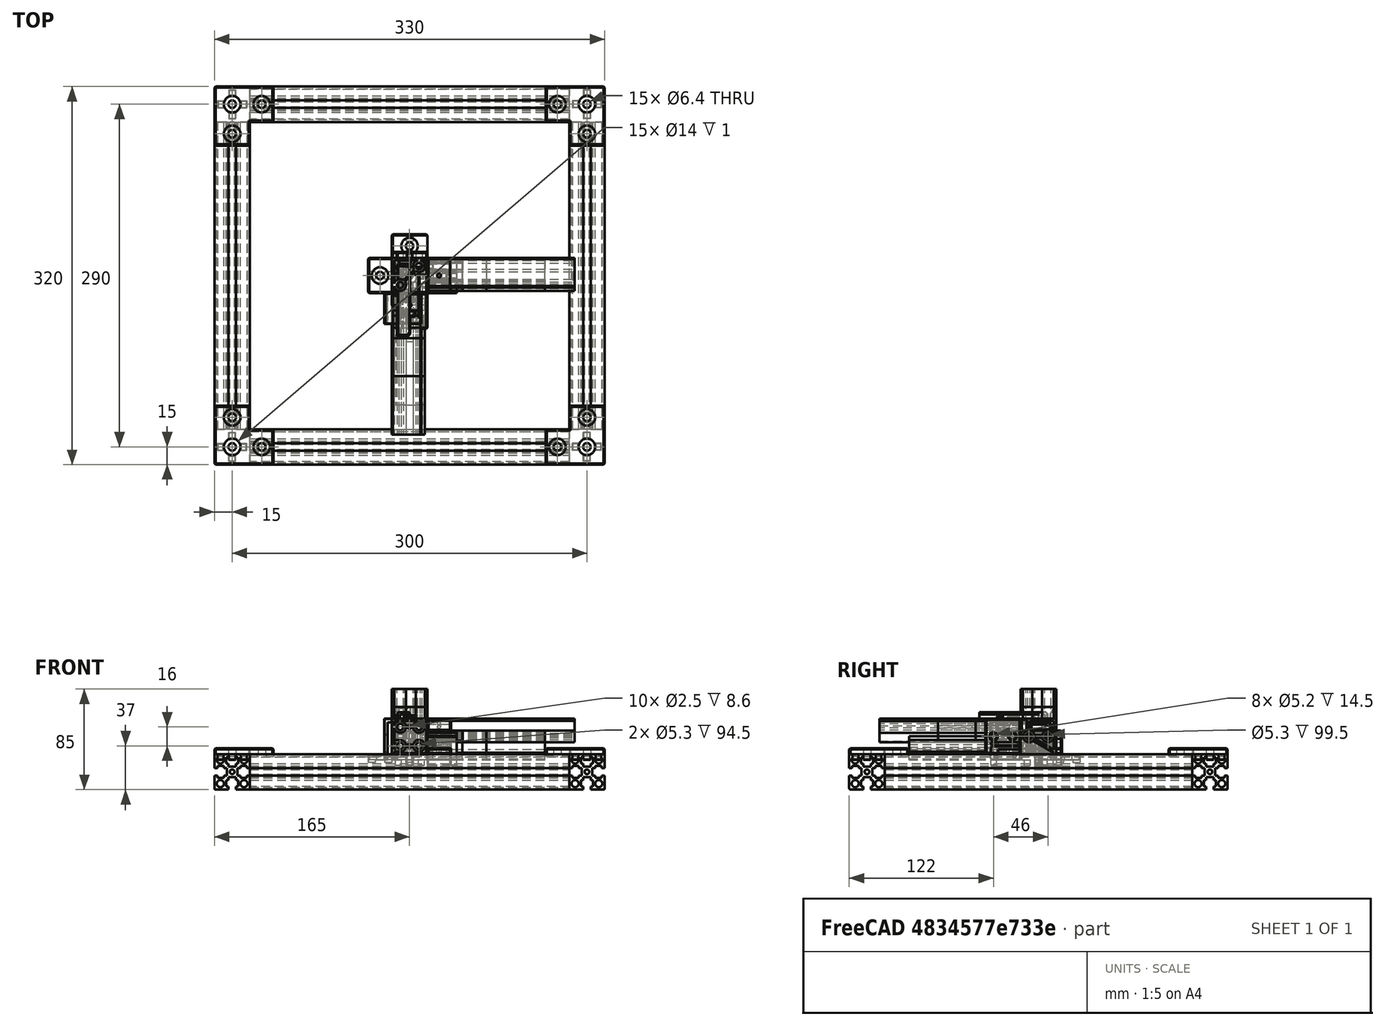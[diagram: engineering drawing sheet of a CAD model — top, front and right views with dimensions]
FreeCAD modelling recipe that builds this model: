
FCSTD DOCUMENT  (FreeCAD 0.18R16146 (Git))
Label: hophat-CF
License: All rights reserved
LicenseURL: http://en.wikipedia.org/wiki/All_rights_reserved
objects: Part::Cylinder×112, Part::MultiFuse×82, Part::Box×79, Part::Chamfer×76, Part::Feature×58, Part::Cut×58, Part::MultiCommon×4, App::DocumentObjectGroup×1
note: 469 computed .brp shape members not serialized (recipe doc carries the construction recipe); baked Part::Feature solids carry a one-line shape summary decoded from their .brp

FEATURE [Part::Feature] Fusion025  label="extrusion-260-003"
  Placement = pos=(-150,-130,350) rot=(-1,0,0;1.5708rad)
  shape: bbox 30 x 260 x 30 mm, 63 faces (baked)
FEATURE [Part::Feature] Fusion032  label="extrusion-270-005"
  Placement = pos=(-135,-145,350) rot=(0,1,0;1.5708rad)
  shape: bbox 270 x 30 x 30 mm, 63 faces (baked)
FEATURE [Part::Feature] Fusion026  label="extrusion-260-004"
  Placement = pos=(150,-130,350) rot=(-1,0,0;1.5708rad)
  shape: bbox 30 x 260 x 30 mm, 63 faces (baked)
FEATURE [Part::Feature] Fusion031  label="extrusion-270-004"
  Placement = pos=(-135,145,350) rot=(0,1,0;1.5708rad)
  shape: bbox 270 x 30 x 30 mm, 63 faces (baked)
FEATURE [Part::MultiFuse] Fusion004003058  label="__top-framr-pref"
  Placement = pos=(0,0,-365) rot=(0,0,1;0rad)
  Shapes = -> [Fusion025,Fusion031,Fusion026,Fusion032]
FEATURE [Part::Feature] Fusion020006007003002004  label="top-joiner-002"
  Placement = pos=(-150,-145,370) rot=(0.707107,0.707107,0;3.14159rad)
  shape: bbox 50 x 50 x 10 mm, 87 faces (baked)
FEATURE [Part::Feature] Fusion020006007003002005  label="top-joiner-003"
  Placement = pos=(-150,145,370) rot=(1,0,0;3.14159rad)
  shape: bbox 50 x 50 x 10 mm, 87 faces (baked)
FEATURE [Part::Feature] Fusion020006007003002006  label="top-joiner-004"
  Placement = pos=(150,145,370) rot=(0.707107,-0.707107,0;3.14159rad)
  shape: bbox 50 x 50 x 10 mm, 87 faces (baked)
FEATURE [Part::Feature] Fusion020006007003002007  label="top-joiner-001"
  Placement = pos=(150,-145,370) rot=(0,1,0;3.14159rad)
  shape: bbox 50 x 50 x 10 mm, 87 faces (baked)
FEATURE [Part::Cylinder] Cylinder
  Angle = 360
  AttacherType = Attacher::AttachEngine3D
  Height = 10
  Radius = 1.25
FEATURE [Part::Cylinder] Cylinder001
  Angle = 360
  AttacherType = Attacher::AttachEngine3D
  Height = 3
  Placement = pos=(0,0,10) rot=(0,0,1;0rad)
  Radius = 3
FEATURE [Part::MultiFuse] Fusion020006007003002009  label="_M3-self-tapping"
  Shapes = -> [Cylinder001,Cylinder]
FEATURE [Part::Cylinder] Cylinder002
  Angle = 360
  AttacherType = Attacher::AttachEngine3D
  Height = 10
  Radius = 1.65
FEATURE [Part::Cylinder] Cylinder003
  Angle = 360
  AttacherType = Attacher::AttachEngine3D
  Height = 3
  Placement = pos=(0,0,10) rot=(0,0,1;0rad)
  Radius = 3
FEATURE [Part::MultiFuse] Fusion020006007003002010  label="_M3-outer-slot"
  Shapes = -> [Cylinder002,Cylinder003]
FEATURE [Part::MultiFuse] Fusion020006007003002008  label="__top-joiner-pref"
  Placement = pos=(0,0,-365) rot=(0,0,1;0rad)
  Shapes = -> [Fusion020006007003002007,Fusion020006007003002004,Fusion020006007003002006,Fusion020006007003002005]
FEATURE [Part::Feature] Fusion020006007003002011  label="top-joiner-005"
  Placement = pos=(-5.7e-14,0,0) rot=(0,1,0;3.14159rad)
  shape: bbox 50 x 50 x 10 mm, 87 faces (baked)
FEATURE [App::DocumentObjectGroup] Group  label="Preference"
  Group = -> [Fusion020006007003002011,Fusion020006007003002008,Fusion020006007003002010,Fusion020006007003002009,Fusion004003058]
FEATURE [Part::Box] Box  label="Cube"
  AttacherType = Attacher::AttachEngine3D
  Height = 30
  Length = 30
  Placement = pos=(-15,-15,0) rot=(0,0,1;0rad)
  Width = 30
FEATURE [Part::Cylinder] Cylinder004
  Angle = 360
  AttacherType = Attacher::AttachEngine3D
  Height = 10
  Placement = pos=(-8,-8,0) rot=(0,0,1;0rad)
  Radius = 2.5
FEATURE [Part::Cylinder] Cylinder005
  Angle = 360
  AttacherType = Attacher::AttachEngine3D
  Height = 10
  Placement = pos=(8,8,0) rot=(0,0,1;0rad)
  Radius = 2.5
FEATURE [Part::Box] Box001  label="Cube001"
  AttacherType = Attacher::AttachEngine3D
  Height = 10
  Length = 10
  Placement = pos=(9.54594,8.83883,20) rot=(0,0,1;0.785398rad)
  Width = 1
FEATURE [Part::Box] Box002  label="Cube002"
  AttacherType = Attacher::AttachEngine3D
  Height = 10
  Length = 10
  Placement = pos=(-15.9099,-16.617,20) rot=(0,0,1;0.785398rad)
  Width = 1
FEATURE [Part::MultiFuse] Fusion020006007003002012
  Shapes = -> [Box002,Box001]
FEATURE [Part::MultiFuse] Fusion
  Placement = pos=(0,0,20) rot=(0,0,1;0rad)
  Shapes = -> [Cylinder004,Cylinder005]
FEATURE [Part::Chamfer] Chamfer
  Base = -> Box
  Edges = 12 edges r=1: [Edge1,Edge2,Edge3,Edge4,Edge5,Edge6,Edge7,Edge8,Edge9,Edge10,Edge11,Edge12]
FEATURE [Part::Cut] Cut
  Base = -> Chamfer
  Tool = -> Fusion
FEATURE [Part::Cut] Cut001
  Base = -> Cut
  Tool = -> Fusion020006007003002012
FEATURE [Part::Cylinder] Cylinder006
  Angle = 360
  AttacherType = Attacher::AttachEngine3D
  Height = 21
  Placement = pos=(-8,5.5,7) rot=(1,0,0;1.5708rad)
  Radius = 2.5
FEATURE [Part::Cylinder] Cylinder007
  Angle = 360
  AttacherType = Attacher::AttachEngine3D
  Height = 21
  Placement = pos=(8,5.5,7) rot=(1,0,0;1.5708rad)
  Radius = 2.5
FEATURE [Part::MultiFuse] Fusion020006007003002013
  Shapes = -> [Cylinder006,Cylinder007]
FEATURE [Part::Cylinder] Cylinder008
  Angle = 360
  AttacherType = Attacher::AttachEngine3D
  Height = 5
  Radius = 6
FEATURE [Part::Cut] Cut002
  Base = -> Cut001
  Tool = -> Cylinder008
FEATURE [Part::Cut] Cut003
  Base = -> Cut002
  Tool = -> Fusion020006007003002013
FEATURE [Part::Box] Box003  label="Cube003"
  AttacherType = Attacher::AttachEngine3D
  Height = 5
  Length = 1
  Placement = pos=(-8.5,-35,0) rot=(0,0,1;0rad)
  Width = 21
FEATURE [Part::Box] Box004  label="Cube004"
  AttacherType = Attacher::AttachEngine3D
  Height = 5
  Length = 1
  Placement = pos=(7.5,-35,0) rot=(0,0,1;0rad)
  Width = 21
FEATURE [Part::Cylinder] Cylinder009
  Angle = 360
  AttacherType = Attacher::AttachEngine3D
  Height = 16
  Placement = pos=(-0.5,8,15) rot=(0,1,0;1.5708rad)
  Radius = 2.6
FEATURE [Part::Cylinder] Cylinder010
  Angle = 360
  AttacherType = Attacher::AttachEngine3D
  Height = 16
  Placement = pos=(-0.5,-8,15) rot=(0,1,0;1.5708rad)
  Radius = 2.6
FEATURE [Part::MultiFuse] Fusion020006007003002015
  Shapes = -> [Cylinder010,Cylinder009]
FEATURE [Part::MultiFuse] Fusion020006007003002016
  Placement = pos=(0,19.5,0) rot=(0,0,1;0rad)
  Shapes = -> [Box003,Box004]
FEATURE [Part::Cut] Cut004
  Base = -> Cut003
  Tool = -> Fusion020006007003002016
FEATURE [Part::Cut] Cut005
  Base = -> Cut004
  Tool = -> Fusion020006007003002015
FEATURE [Part::Chamfer] Chamfer001
  Base = -> Cut005
  Edges = 14 edges r=1: [Edge24,Edge25,Edge27,Edge29,Edge30,Edge32,Edge39,Edge45,Edge61,Edge62,Edge64,Edge67,Edge138,Edge139]
FEATURE [Part::Chamfer] Chamfer002
  Base = -> Chamfer001
  Edges = 9 edges r=0.4: [Edge52,Edge70,Edge74,Edge78,Edge115,Edge152,Edge156,Edge157,Edge161]
FEATURE [Part::Feature] Fusion020006007003002009001  label="_M3-self-tapping001"
  Placement = pos=(-6,0,15) rot=(0,-1,0;1.5708rad)
  shape: bbox 13 x 6 x 6 mm, 5 faces (baked)
FEATURE [Part::Feature] Fusion020006007003002009002  label="_M3-self-tapping002"
  Placement = pos=(0,6,7) rot=(-1,0,0;1.5708rad)
  shape: bbox 6 x 13 x 6 mm, 5 faces (baked)
FEATURE [Part::Feature] Fusion020006007003002009003  label="_M3-self-tapping003"
  Placement = pos=(0,6,23) rot=(-1,0,0;1.5708rad)
  shape: bbox 6 x 13 x 6 mm, 5 faces (baked)
FEATURE [Part::MultiFuse] Fusion020006007003002009004
  Shapes = -> [Fusion020006007003002009003,Fusion020006007003002009002,Fusion020006007003002009001]
FEATURE [Part::Cut] Cut006
  Base = -> Chamfer002
  Tool = -> Fusion020006007003002009004
FEATURE [Part::Chamfer] Chamfer003  label="bottom-cube"
  Base = -> Cut006
  Edges = 3 edges r=0.4: [Edge54,Edge107,Edge108]
FEATURE [Part::Cylinder] Cylinder011
  Angle = 360
  AttacherType = Attacher::AttachEngine3D
  Height = 10
  Placement = pos=(8,8,0) rot=(0,0,1;0rad)
  Radius = 2.5
FEATURE [Part::Cylinder] Cylinder012
  Angle = 360
  AttacherType = Attacher::AttachEngine3D
  Height = 10
  Placement = pos=(-8,-8,0) rot=(0,0,1;0rad)
  Radius = 2.5
FEATURE [Part::Box] Box005  label="Cube005"
  AttacherType = Attacher::AttachEngine3D
  Height = 30
  Length = 30
  Placement = pos=(-15,-15,0) rot=(0,0,1;0rad)
  Width = 30
FEATURE [Part::Box] Box006  label="Cube006"
  AttacherType = Attacher::AttachEngine3D
  Height = 10
  Length = 10
  Placement = pos=(9.89949,9.19239,0) rot=(0,0,1;0.785398rad)
  Width = 1
FEATURE [Part::Box] Box007  label="Cube007"
  AttacherType = Attacher::AttachEngine3D
  Height = 10
  Length = 10
  Placement = pos=(-16.2635,-16.9706,0) rot=(0,0,1;0.785398rad)
  Width = 1
FEATURE [Part::Cylinder] Cylinder013
  Angle = 360
  AttacherType = Attacher::AttachEngine3D
  Height = 21
  Placement = pos=(-8,5.5,23) rot=(1,0,0;1.5708rad)
  Radius = 2.5
FEATURE [Part::Cylinder] Cylinder014
  Angle = 360
  AttacherType = Attacher::AttachEngine3D
  Height = 21
  Placement = pos=(8,5.5,23) rot=(1,0,0;1.5708rad)
  Radius = 2.5
FEATURE [Part::Cylinder] Cylinder015
  Angle = 360
  AttacherType = Attacher::AttachEngine3D
  Height = 16
  Placement = pos=(-0.5,8,15) rot=(0,1,0;1.5708rad)
  Radius = 2.6
FEATURE [Part::Cylinder] Cylinder016
  Angle = 360
  AttacherType = Attacher::AttachEngine3D
  Height = 16
  Placement = pos=(-0.5,-8,15) rot=(0,1,0;1.5708rad)
  Radius = 2.6
FEATURE [Part::Box] Box008  label="Cube008"
  AttacherType = Attacher::AttachEngine3D
  Height = 6
  Length = 1
  Placement = pos=(-8.5,-15.5,25) rot=(0,0,1;0rad)
  Width = 21
FEATURE [Part::Box] Box009  label="Cube009"
  AttacherType = Attacher::AttachEngine3D
  Height = 6
  Length = 1
  Placement = pos=(7.5,-15.5,25) rot=(0,0,1;0rad)
  Width = 21
FEATURE [Part::MultiFuse] Fusion020006007003002009005
  Shapes = -> [Cylinder016,Box007,Cylinder014,Box009,Cylinder012,Cylinder011,Cylinder013,Cylinder015,Box006,Box008]
FEATURE [Part::Chamfer] Chamfer004
  Base = -> Box005
  Edges = 12 edges r=1: [Edge1,Edge2,Edge3,Edge4,Edge5,Edge6,Edge7,Edge8,Edge9,Edge10,Edge11,Edge12]
FEATURE [Part::Cut] Cut007
  Base = -> Chamfer004
  Tool = -> Fusion020006007003002009005
FEATURE [Part::Feature] Fusion020006007003002009006  label="_M3-self-tapping004"
  Placement = pos=(-6,0,15) rot=(0,-1,0;1.5708rad)
  shape: bbox 13 x 6 x 6 mm, 5 faces (baked)
FEATURE [Part::Feature] Fusion020006007003002009007  label="_M3-self-tapping005"
  Placement = pos=(0,6,7) rot=(-1,0,0;1.5708rad)
  shape: bbox 6 x 13 x 6 mm, 5 faces (baked)
FEATURE [Part::Feature] Fusion020006007003002009008  label="_M3-self-tapping006"
  Placement = pos=(0,6,23) rot=(-1,0,0;1.5708rad)
  shape: bbox 6 x 13 x 6 mm, 5 faces (baked)
FEATURE [Part::MultiFuse] Fusion020006007003002009009
  Shapes = -> [Fusion020006007003002009008,Fusion020006007003002009007,Fusion020006007003002009006]
FEATURE [Part::Cut] Cut008
  Base = -> Cut007
  Tool = -> Fusion020006007003002009009
FEATURE [Part::Chamfer] Chamfer005
  Base = -> Cut008
  Edges = 14 edges r=1: [Edge26,Edge31,Edge39,Edge41,Edge42,Edge44,Edge46,Edge47,Edge51,Edge52,Edge54,Edge58,Edge138,Edge139]
FEATURE [Part::Chamfer] Chamfer006  label="top-cube-base"
  Base = -> Chamfer005
  Edges = 11 edges r=0.4: [Edge26,Edge53,Edge71,Edge72,Edge75,Edge79,Edge83,Edge160,Edge164,Edge165,Edge169]
FEATURE [Part::Feature] Chamfer006001  label="top-cube-base001"
  shape: bbox 30 x 30 x 30 mm, 85 faces (baked)
FEATURE [Part::Box] Box010  label="Cube010"
  AttacherType = Attacher::AttachEngine3D
  Height = 10
  Length = 10.5
  Placement = pos=(-10,-15,27.5) rot=(0,0,1;0rad)
  Width = 25
FEATURE [Part::Box] Box012  label="Cube012"
  AttacherType = Attacher::AttachEngine3D
  Height = 2
  Length = 10
  Placement = pos=(-10,-50,28) rot=(0,0,1;0rad)
  Width = 54
FEATURE [Part::Box] Box013  label="Cube013"
  AttacherType = Attacher::AttachEngine3D
  Height = 2
  Length = 10
  Placement = pos=(-10,-50,33.5) rot=(0,0,1;0rad)
  Width = 54
FEATURE [Part::Cylinder] Cylinder017
  Angle = 360
  AttacherType = Attacher::AttachEngine3D
  Height = 10
  Placement = pos=(-10,4,31.75) rot=(0,1,0;1.5708rad)
  Radius = 3.75
FEATURE [Part::Box] Box014  label="Cube014"
  AttacherType = Attacher::AttachEngine3D
  Height = 7.5
  Length = 2
  Placement = pos=(-10,-50,28) rot=(0,0,1;0rad)
  Width = 54
FEATURE [Part::Cylinder] Cylinder018
  Angle = 360
  AttacherType = Attacher::AttachEngine3D
  Height = 10
  Placement = pos=(-10,4,31.75) rot=(0,1,0;1.5708rad)
  Radius = 1.65
FEATURE [Part::Cylinder] Cylinder019
  Angle = 360
  AttacherType = Attacher::AttachEngine3D
  Height = 10
  Placement = pos=(-16,4,31.75) rot=(0,1,0;1.5708rad)
  Radius = 2
FEATURE [Part::MultiFuse] Fusion020006007003002009010
  Shapes = -> [Box014,Cylinder017,Box013,Box012]
FEATURE [Part::Chamfer] Chamfer006002
  Base = -> Fusion020006007003002009010
  Edges = 2 edges r=2: [Edge16,Edge51]
FEATURE [Part::Chamfer] Chamfer006003
  Base = -> Chamfer006002
  Edges = 3 edges r=0.4: [Edge21,Edge23,Edge41]
FEATURE [Part::Cut] Cut010  label="top-arm"
  Base = -> Chamfer006003
  Tool = -> Cylinder018
FEATURE [Part::Box] Box015  label="Cube015"
  AttacherType = Attacher::AttachEngine3D
  Height = 7
  Length = 5
  Placement = pos=(-15,0,29) rot=(0,0,1;0rad)
  Width = 8
FEATURE [Part::Chamfer] Chamfer006004
  Base = -> Box015
  Edges = 2 edges r=2: [Edge10,Edge12]
FEATURE [Part::Chamfer] Chamfer006005
  Base = -> Chamfer006004
  Edges = 10 edges r=0.4: [Edge1,Edge2,Edge4,Edge5,Edge6,Edge7,Edge11,Edge15,Edge16,Edge18]
FEATURE [Part::Box] Box016  label="Cube016"
  AttacherType = Attacher::AttachEngine3D
  Height = 10
  Length = 10
  Placement = pos=(-9,10,29) rot=(0,0,1;0rad)
  Width = 5
FEATURE [Part::Chamfer] Chamfer006006
  Base = -> Box016
  Edges = 1 edges: [Edge10 r1=5 r2=3]
FEATURE [Part::Chamfer] Chamfer006007
  Base = -> Chamfer006006
  Edges = 10 edges r=0.4: [Edge1,Edge2,Edge4,Edge5,Edge6,Edge9,Edge10,Edge13,Edge14,Edge15]
FEATURE [Part::MultiFuse] Fusion020006007003002009011
  Shapes = -> [Chamfer006001,Chamfer006005,Chamfer006007]
FEATURE [Part::Cut] Cut011
  Base = -> Fusion020006007003002009011
  Tool = -> Box010
FEATURE [Part::Cylinder] Cylinder020
  Angle = 360
  AttacherType = Attacher::AttachEngine3D
  Height = 17
  Placement = pos=(-7.1e-15,4,31.75) rot=(0,1,0;1.5708rad)
  Radius = 3.75
FEATURE [Part::Cut] Cut012
  Base = -> Cut011
  Tool = -> Cylinder019
FEATURE [Part::Cut] Cut013  label="top-back-cube"
  Base = -> Cut012
  Tool = -> Cylinder020
FEATURE [Part::Cylinder] Cylinder021
  Angle = 360
  AttacherType = Attacher::AttachEngine3D
  Height = 25
  Placement = pos=(-8,-15,7) rot=(1,0,0;1.5708rad)
  Radius = 2.5
FEATURE [Part::Cylinder] Cylinder022
  Angle = 360
  AttacherType = Attacher::AttachEngine3D
  Height = 25
  Placement = pos=(8,-15,7) rot=(1,0,0;1.5708rad)
  Radius = 2.5
FEATURE [Part::Box] Box017  label="Cube017"
  AttacherType = Attacher::AttachEngine3D
  Height = 12
  Length = 30
  Placement = pos=(-15,-40,0) rot=(0,0,1;0rad)
  Width = 25
FEATURE [Part::Box] Box018  label="Cube018"
  AttacherType = Attacher::AttachEngine3D
  Height = 6
  Length = 30
  Placement = pos=(-15,-40,-5) rot=(0,0,1;0rad)
  Width = 4.5
FEATURE [Part::Box] Box019  label="Cube019"
  AttacherType = Attacher::AttachEngine3D
  Height = 5
  Length = 6
  Placement = pos=(-3,-40,-10) rot=(0,0,1;0rad)
  Width = 4.5
FEATURE [Part::Box] Box020  label="Cube020"
  AttacherType = Attacher::AttachEngine3D
  Height = 1
  Length = 5
  Placement = pos=(-15,-40,6.5) rot=(0,0,1;0rad)
  Width = 25
FEATURE [Part::Box] Box021  label="Cube021"
  AttacherType = Attacher::AttachEngine3D
  Height = 1
  Length = 5
  Placement = pos=(10,-40,6.5) rot=(0,0,1;0rad)
  Width = 25
FEATURE [Part::Chamfer] Chamfer006011
  Base = -> Box019
  Edges = 2 edges r=1: [Edge4,Edge8]
FEATURE [Part::Cylinder] Cylinder023
  Angle = 360
  AttacherType = Attacher::AttachEngine3D
  Height = 25
  Placement = pos=(15,8,15) rot=(0,1,0;1.5708rad)
  Radius = 2.5
FEATURE [Part::Cylinder] Cylinder024
  Angle = 360
  AttacherType = Attacher::AttachEngine3D
  Height = 25
  Placement = pos=(15,-8,15) rot=(0,1,0;1.5708rad)
  Radius = 2.5
FEATURE [Part::Box] Box022  label="Cube022"
  AttacherType = Attacher::AttachEngine3D
  Height = 20
  Length = 25
  Placement = pos=(15,-15,0) rot=(0,0,1;0rad)
  Width = 30
FEATURE [Part::Box] Box023  label="Cube023"
  AttacherType = Attacher::AttachEngine3D
  Height = 6
  Length = 4.5
  Placement = pos=(35.5,-15,-5) rot=(0,0,1;0rad)
  Width = 30
FEATURE [Part::Box] Box024  label="Cube024"
  AttacherType = Attacher::AttachEngine3D
  Height = 5
  Length = 4.5
  Placement = pos=(35.5,-3,-10) rot=(0,0,1;0rad)
  Width = 6
FEATURE [Part::Box] Box025  label="Cube025"
  AttacherType = Attacher::AttachEngine3D
  Height = 1
  Length = 25
  Placement = pos=(15,-15,14.5) rot=(0,0,1;0rad)
  Width = 6
FEATURE [Part::Box] Box026  label="Cube026"
  AttacherType = Attacher::AttachEngine3D
  Height = 1
  Length = 25
  Placement = pos=(15,9,14.5) rot=(0,0,1;0rad)
  Width = 6
FEATURE [Part::Chamfer] Chamfer006015
  Base = -> Box023
  Edges = 2 edges r=1: [Edge9,Edge11]
FEATURE [Part::Chamfer] Chamfer006016
  Base = -> Box024
  Edges = 2 edges r=1: [Edge9,Edge11]
FEATURE [Part::Chamfer] Chamfer006017
  Base = -> Box022
  Edges = 2 edges r=2: [Edge10,Edge12]
FEATURE [Part::Chamfer] Chamfer006018
  Base = -> Chamfer006017
  Edges = 2 edges r=1: [Edge9,Edge12]
FEATURE [Part::MultiFuse] Fusion020006007003002009014
  Shapes = -> [Chamfer006018,Chamfer006015,Chamfer006016]
FEATURE [Part::MultiFuse] Fusion020006007003002009015
  Shapes = -> [Cylinder024,Box025,Cylinder023,Box026]
FEATURE [Part::Cut] Cut015
  Base = -> Fusion020006007003002009014
  Tool = -> Fusion020006007003002009015
FEATURE [Part::Cylinder] Cylinder025
  Angle = 360
  AttacherType = Attacher::AttachEngine3D
  Height = 5
  Placement = pos=(25,0,0) rot=(0,0,1;0rad)
  Radius = 6
FEATURE [Part::Cylinder] Cylinder026
  Angle = 360
  AttacherType = Attacher::AttachEngine3D
  Height = 5
  Placement = pos=(0,-25,0) rot=(0,0,1;0rad)
  Radius = 6
FEATURE [Part::Cut] Cut016
  Base = -> Cut015
  Tool = -> Cylinder025
FEATURE [Part::MultiFuse] Fusion020006007003002009016
  Shapes = -> [Box021,Cylinder022,Box020,Cylinder021]
FEATURE [Part::Chamfer] Chamfer006019
  Base = -> Box017
  Edges = 2 edges r=2: [Edge2,Edge6]
FEATURE [Part::Chamfer] Chamfer006020
  Base = -> Chamfer006019
  Edges = 2 edges r=1: [Edge3,Edge13]
FEATURE [Part::Chamfer] Chamfer006021
  Base = -> Box018
  Edges = 2 edges r=1: [Edge4,Edge8]
FEATURE [Part::MultiFuse] Fusion020006007003002009017
  Shapes = -> [Chamfer006021,Chamfer006020,Chamfer006011]
FEATURE [Part::Cut] Cut017
  Base = -> Fusion020006007003002009017
  Tool = -> Fusion020006007003002009016
FEATURE [Part::Chamfer] Chamfer006022
  Base = -> Cut017
  Edges = 14 edges r=1: [Edge40,Edge41,Edge42,Edge48,Edge49,Edge50,Edge51,Edge52,Edge55,Edge56,Edge57,Edge63,Edge64,Edge65]
FEATURE [Part::Chamfer] Chamfer006023  label="fb-stopper"
  Base = -> Cut016
  Edges = 16 edges r=1: [Edge2,Edge3,Edge4,Edge5,Edge11,Edge12,Edge13,Edge14,Edge24,Edge26,Edge27,Edge29,Edge41,Edge44,Edge45,Edge48]
FEATURE [Part::Cut] Cut018  label="side-stopper"
  Base = -> Chamfer006022
  Tool = -> Cylinder026
FEATURE [Part::Cylinder] Cylinder027
  Angle = 360
  AttacherType = Attacher::AttachEngine3D
  Height = 20
  Placement = pos=(8,-15,7) rot=(1,0,0;1.5708rad)
  Radius = 2.6
FEATURE [Part::Cylinder] Cylinder028
  Angle = 360
  AttacherType = Attacher::AttachEngine3D
  Height = 20
  Placement = pos=(-8,-15,7) rot=(1,0,0;1.5708rad)
  Radius = 2.6
FEATURE [Part::Cylinder] Cylinder029
  Angle = 360
  AttacherType = Attacher::AttachEngine3D
  Height = 20
  Placement = pos=(-8,-15,7) rot=(1,0,0;1.5708rad)
  Radius = 6
FEATURE [Part::Cylinder] Cylinder030
  Angle = 360
  AttacherType = Attacher::AttachEngine3D
  Height = 20
  Placement = pos=(8,-15,7) rot=(1,0,0;1.5708rad)
  Radius = 6
FEATURE [Part::Chamfer] Chamfer006025
  Base = -> Cylinder029
  Edges = 2 edges r=1: [Edge1,Edge3]
FEATURE [Part::Chamfer] Chamfer006026
  Base = -> Cylinder030
  Edges = 2 edges r=1: [Edge1,Edge3]
FEATURE [Part::MultiFuse] Fusion020006007003002009018003
  Shapes = -> [Cylinder028,Cylinder027]
FEATURE [Part::Feature] Fusion020006007003002009018004001  label="Fusion020006007003002009018005"
  shape: bbox 30 x 20 x 25 mm, 10 faces (baked)
FEATURE [Part::Chamfer] Chamfer006027
  Base = -> Fusion020006007003002009018004001
  Edges = 23 edges r=1: [Edge1,Edge2,Edge3,Edge4,Edge5,Edge6,Edge7,Edge8,Edge9,Edge10,Edge11,Edge12,Edge14,Edge15,Edge16,Edge17,Edge18,Edge19,Edge20,Edge21,Edge22,Edge23,Edge24]
FEATURE [Part::MultiFuse] Fusion020006007003002009018004002
  Shapes = -> [Chamfer006027,Chamfer006025,Chamfer006026]
FEATURE [Part::Cut] Cut019
  Base = -> Fusion020006007003002009018004002
  Tool = -> Fusion020006007003002009018003
FEATURE [Part::Feature] Cut019001  label="Cut020"
  shape: bbox 30 x 20 x 25 mm, 59 faces (baked)
FEATURE [Part::Chamfer] Chamfer006028
  Base = -> Cut019001
  Edges = 4 edges r=1: [Edge120,Edge121,Edge123,Edge125]
FEATURE [Part::Feature] Fusion020006007003002009018004003  label="_M3-self-tapping007"
  Placement = pos=(-6,-25,15) rot=(0,-1,0;1.5708rad)
  shape: bbox 13 x 6 x 6 mm, 5 faces (baked)
FEATURE [Part::Cut] Cut019002  label="bottom-side-mid-block"
  Base = -> Chamfer006028
  Tool = -> Fusion020006007003002009018004003
FEATURE [Part::Cylinder] Cylinder031
  Angle = 360
  AttacherType = Attacher::AttachEngine3D
  Height = 20
  Placement = pos=(15,8,15) rot=(0,1,0;1.5708rad)
  Radius = 2.6
FEATURE [Part::Cylinder] Cylinder032
  Angle = 360
  AttacherType = Attacher::AttachEngine3D
  Height = 20
  Placement = pos=(15,-8,15) rot=(0,1,0;1.5708rad)
  Radius = 2.6
FEATURE [Part::Box] Box027  label="Cube027"
  AttacherType = Attacher::AttachEngine3D
  Height = 5
  Length = 20
  Placement = pos=(15,-15,0) rot=(0,0,1;0rad)
  Width = 30
FEATURE [Part::Box] Box028  label="Cube028"
  AttacherType = Attacher::AttachEngine3D
  Height = 5
  Length = 20
  Placement = pos=(15,10,-5) rot=(0,0,1;0rad)
  Width = 5
FEATURE [Part::Box] Box029  label="Cube029"
  AttacherType = Attacher::AttachEngine3D
  Height = 15
  Length = 20
  Placement = pos=(15,10,0) rot=(0,0,1;0rad)
  Width = 5
FEATURE [Part::MultiFuse] Fusion020006007003002009018004004
  Shapes = -> [Box029,Box027,Box028]
FEATURE [Part::Feature] Fusion020006007003002009018004004001  label="Fusion020006007003002009018004005"
  shape: bbox 20 x 30 x 20 mm, 10 faces (baked)
FEATURE [Part::Chamfer] Chamfer006029
  Base = -> Fusion020006007003002009018004004001
  Edges = 22 edges r=1: [Edge1,Edge3,Edge4,Edge5,Edge6,Edge7,Edge8,Edge10,Edge11,Edge12,Edge13,Edge14,Edge15,Edge16,Edge17,Edge18,Edge19,Edge20,Edge21,Edge22,Edge23,Edge24]
FEATURE [Part::Cylinder] Cylinder033
  Angle = 360
  AttacherType = Attacher::AttachEngine3D
  Height = 20
  Placement = pos=(15,-8,15) rot=(0,1,0;1.5708rad)
  Radius = 6
FEATURE [Part::Cylinder] Cylinder034
  Angle = 360
  AttacherType = Attacher::AttachEngine3D
  Height = 20
  Placement = pos=(15,8,15) rot=(0,1,0;1.5708rad)
  Radius = 6
FEATURE [Part::Chamfer] Chamfer006030
  Base = -> Cylinder033
  Edges = 2 edges r=1: [Edge1,Edge3]
FEATURE [Part::Chamfer] Chamfer006031
  Base = -> Cylinder034
  Edges = 2 edges r=1: [Edge1,Edge3]
FEATURE [Part::Box] Box030  label="Cube030"
  AttacherType = Attacher::AttachEngine3D
  Height = 8
  Length = 20
  Placement = pos=(15,-10,4) rot=(0,0,1;0rad)
  Width = 4
FEATURE [Part::Chamfer] Chamfer006032
  Base = -> Box030
  Edges = 4 edges r=1: [Edge1,Edge3,Edge5,Edge7]
FEATURE [Part::MultiFuse] Fusion020006007003002009018004004002
  Shapes = -> [Chamfer006032,Chamfer006029]
FEATURE [Part::MultiFuse] Fusion020006007003002009018004004003
  Shapes = -> [Chamfer006030,Chamfer006031,Fusion020006007003002009018004004002]
FEATURE [Part::MultiFuse] Fusion020006007003002009018004004004
  Shapes = -> [Cylinder032,Cylinder031]
FEATURE [Part::Cut] Cut019003
  Base = -> Fusion020006007003002009018004004003
  Tool = -> Fusion020006007003002009018004004004
FEATURE [Part::Feature] Cut019003001  label="Cut019004"
  shape: bbox 20 x 30 x 26 mm, 59 faces (baked)
FEATURE [Part::Chamfer] Chamfer006033
  Base = -> Cut019003001
  Edges = 4 edges r=1: [Edge120,Edge121,Edge122,Edge124]
FEATURE [Part::Feature] Fusion020006007003002009018004004005  label="_M3-self-tapping008"
  Placement = pos=(25,6,7) rot=(-1,0,0;1.5708rad)
  shape: bbox 6 x 13 x 6 mm, 5 faces (baked)
FEATURE [Part::Cut] Cut019003002  label="bottom-fb-mid-block"
  Base = -> Chamfer006033
  Tool = -> Fusion020006007003002009018004004005
FEATURE [Part::Cylinder] Cylinder035
  Angle = 360
  AttacherType = Attacher::AttachEngine3D
  Height = 94.5
  Placement = pos=(8,-15,7) rot=(1,0,0;1.5708rad)
  Radius = 2.65
FEATURE [Part::Cylinder] Cylinder036
  Angle = 360
  AttacherType = Attacher::AttachEngine3D
  Height = 94.5
  Placement = pos=(-8,-15,7) rot=(1,0,0;1.5708rad)
  Radius = 2.65
FEATURE [Part::Box] Box031  label="Cube031"
  AttacherType = Attacher::AttachEngine3D
  Height = 20
  Length = 2
  Placement = pos=(-15,-109.5,-5) rot=(0,0,1;0rad)
  Width = 94.5
FEATURE [Part::Box] Box032  label="Cube032"
  AttacherType = Attacher::AttachEngine3D
  Height = 2
  Length = 24
  Placement = pos=(-15,-109.5,6) rot=(0,0,1;0rad)
  Width = 94.5
FEATURE [Part::Cylinder] Cylinder037
  Angle = 360
  AttacherType = Attacher::AttachEngine3D
  Height = 94.5
  Placement = pos=(-8,-15,7) rot=(1,0,0;1.5708rad)
  Radius = 5
FEATURE [Part::Cylinder] Cylinder038
  Angle = 360
  AttacherType = Attacher::AttachEngine3D
  Height = 94.5
  Placement = pos=(8,-15,7) rot=(1,0,0;1.5708rad)
  Radius = 5
FEATURE [Part::Box] Box033  label="Cube033"
  AttacherType = Attacher::AttachEngine3D
  Height = 2
  Length = 6
  Placement = pos=(-14,-109.5,2) rot=(0,0,1;0rad)
  Width = 94.5
FEATURE [Part::MultiFuse] Fusion020006007003002009018004004007
  Shapes = -> [Cylinder037,Cylinder038]
FEATURE [Part::MultiFuse] Fusion020006007003002009018004004009
  Shapes = -> [Cylinder036,Cylinder035]
FEATURE [Part::Chamfer] Chamfer006034
  Base = -> Box031
  Edges = 1 edges r=1: [Edge4]
FEATURE [Part::Cylinder] Cylinder039
  Angle = 360
  AttacherType = Attacher::AttachEngine3D
  Height = 149.5
  Placement = pos=(15,8,15) rot=(0,1,0;1.5708rad)
  Radius = 2.65
FEATURE [Part::Cylinder] Cylinder040
  Angle = 360
  AttacherType = Attacher::AttachEngine3D
  Height = 149.5
  Placement = pos=(15,-8,15) rot=(0,1,0;1.5708rad)
  Radius = 2.65
FEATURE [Part::Box] Box036  label="Cube036"
  AttacherType = Attacher::AttachEngine3D
  Height = 24
  Length = 149.5
  Placement = pos=(15,13,-5) rot=(0,0,1;0rad)
  Width = 2
FEATURE [Part::Box] Box037  label="Cube037"
  AttacherType = Attacher::AttachEngine3D
  Height = 2
  Length = 149.5
  Placement = pos=(15,-5,14) rot=(0,0,1;0rad)
  Width = 19
FEATURE [Part::Cylinder] Cylinder041
  Angle = 360
  AttacherType = Attacher::AttachEngine3D
  Height = 149.5
  Placement = pos=(15,-8,15) rot=(0,1,0;1.5708rad)
  Radius = 5
FEATURE [Part::Cylinder] Cylinder042
  Angle = 360
  AttacherType = Attacher::AttachEngine3D
  Height = 149.5
  Placement = pos=(15,8,15) rot=(0,1,0;1.5708rad)
  Radius = 5
FEATURE [Part::Box] Box038  label="Cube038"
  AttacherType = Attacher::AttachEngine3D
  Height = 2
  Length = 149.5
  Placement = pos=(15,-6,12.2679) rot=(-1,0,0;0.523599rad)
  Width = 23
FEATURE [Part::Box] Box039  label="Cube039"
  AttacherType = Attacher::AttachEngine3D
  Height = 2
  Length = 29.5
  Placement = pos=(15,-6,12.2679) rot=(-1,0,0;0.523599rad)
  Width = 23
FEATURE [Part::Cylinder] Cylinder043
  Angle = 360
  AttacherType = Attacher::AttachEngine3D
  Height = 29.5
  Placement = pos=(15,8,15) rot=(0,1,0;1.5708rad)
  Radius = 5
FEATURE [Part::Cylinder] Cylinder044
  Angle = 360
  AttacherType = Attacher::AttachEngine3D
  Height = 29.5
  Placement = pos=(15,-8,15) rot=(0,1,0;1.5708rad)
  Radius = 5
FEATURE [Part::Box] Box040  label="Cube040"
  AttacherType = Attacher::AttachEngine3D
  Height = 2
  Length = 29.5
  Placement = pos=(15,-5,14) rot=(0,0,1;0rad)
  Width = 19
FEATURE [Part::Box] Box041  label="Cube041"
  AttacherType = Attacher::AttachEngine3D
  Height = 21
  Length = 29.5
  Placement = pos=(15,13,-5) rot=(0,0,1;0rad)
  Width = 2
FEATURE [Part::Cylinder] Cylinder045
  Angle = 360
  AttacherType = Attacher::AttachEngine3D
  Height = 29.5
  Placement = pos=(15,-8,15) rot=(0,1,0;1.5708rad)
  Radius = 2.65
FEATURE [Part::Cylinder] Cylinder046
  Angle = 360
  AttacherType = Attacher::AttachEngine3D
  Height = 29.5
  Placement = pos=(15,8,15) rot=(0,1,0;1.5708rad)
  Radius = 2.65
FEATURE [Part::MultiFuse] Fusion020006007003002009018004004011
  Shapes = -> [Cylinder044,Box040,Box039,Cylinder043,Box041]
FEATURE [Part::Chamfer] Chamfer006035
  Base = -> Fusion020006007003002009018004004011
  Edges = 1 edges r=1: [Edge79]
FEATURE [Part::MultiFuse] Fusion020006007003002009018004004012
  Shapes = -> [Cylinder046,Cylinder045]
FEATURE [Part::Cut] Cut019003004  label="bottom-back-30mm-wall"
  Base = -> Chamfer006035
  Tool = -> Fusion020006007003002009018004004012
FEATURE [Part::Box] Box042  label="Cube042"
  AttacherType = Attacher::AttachEngine3D
  Height = 2
  Length = 6
  Placement = pos=(-14,-109.5,10) rot=(0,0,1;0rad)
  Width = 94.5
FEATURE [Part::MultiFuse] Fusion020006007003002009018004004013
  Shapes = -> [Box042,Fusion020006007003002009018004004007,Box033,Box032,Chamfer006034]
FEATURE [Part::Cut] Cut019003005  label="bottom-side-95mm-wall"
  Base = -> Fusion020006007003002009018004004013
  Tool = -> Fusion020006007003002009018004004009
FEATURE [Part::Box] Box043  label="Cube043"
  AttacherType = Attacher::AttachEngine3D
  Height = 2
  Length = 99.5
  Placement = pos=(15,-6,12.2679) rot=(-1,0,0;0.523599rad)
  Width = 23
FEATURE [Part::Box] Box044  label="Cube044"
  AttacherType = Attacher::AttachEngine3D
  Height = 24
  Length = 99.5
  Placement = pos=(15,13,-5) rot=(0,0,1;0rad)
  Width = 2
FEATURE [Part::Cylinder] Cylinder047
  Angle = 360
  AttacherType = Attacher::AttachEngine3D
  Height = 99.5
  Placement = pos=(15,8,15) rot=(0,1,0;1.5708rad)
  Radius = 5
FEATURE [Part::Box] Box045  label="Cube045"
  AttacherType = Attacher::AttachEngine3D
  Height = 2
  Length = 99.5
  Placement = pos=(15,-5,14) rot=(0,0,1;0rad)
  Width = 19
FEATURE [Part::Cylinder] Cylinder048
  Angle = 360
  AttacherType = Attacher::AttachEngine3D
  Height = 99.5
  Placement = pos=(15,8,15) rot=(0,1,0;1.5708rad)
  Radius = 2.65
FEATURE [Part::Cylinder] Cylinder049
  Angle = 360
  AttacherType = Attacher::AttachEngine3D
  Height = 99.5
  Placement = pos=(15,-8,15) rot=(0,1,0;1.5708rad)
  Radius = 2.65
FEATURE [Part::Cylinder] Cylinder050
  Angle = 360
  AttacherType = Attacher::AttachEngine3D
  Height = 99.5
  Placement = pos=(15,-8,15) rot=(0,1,0;1.5708rad)
  Radius = 5
FEATURE [Part::MultiFuse] Fusion020006007003002009018004004014
  Shapes = -> [Cylinder042,Cylinder041,Box038,Box037,Box036]
FEATURE [Part::Chamfer] Chamfer006036
  Base = -> Fusion020006007003002009018004004014
  Edges = 1 edges r=1: [Edge97]
FEATURE [Part::MultiFuse] Fusion020006007003002009018004004015
  Shapes = -> [Cylinder040,Cylinder039]
FEATURE [Part::Cut] Cut019003006  label="bottom-back-150mm-wall"
  Base = -> Chamfer006036
  Tool = -> Fusion020006007003002009018004004015
FEATURE [Part::MultiFuse] Fusion020006007003002009018004004016
  Shapes = -> [Cylinder050,Cylinder047,Box043,Box044,Box045]
FEATURE [Part::Chamfer] Chamfer006037
  Base = -> Fusion020006007003002009018004004016
  Edges = 1 edges r=1: [Edge83]
FEATURE [Part::MultiFuse] Fusion020006007003002009018004004017
  Shapes = -> [Cylinder049,Cylinder048]
FEATURE [Part::Cut] Cut019003007  label="bottom-fb-100mm-wall"
  Base = -> Chamfer006037
  Tool = -> Fusion020006007003002009018004004017
FEATURE [Part::Cylinder] Cylinder051
  Angle = 360
  AttacherType = Attacher::AttachEngine3D
  Height = 30
  Placement = pos=(15,8,15) rot=(0,1,0;1.5708rad)
  Radius = 5
FEATURE [Part::Cylinder] Cylinder052
  Angle = 360
  AttacherType = Attacher::AttachEngine3D
  Height = 30
  Placement = pos=(15,-8,15) rot=(0,1,0;1.5708rad)
  Radius = 5
FEATURE [Part::Cylinder] Cylinder053
  Angle = 360
  AttacherType = Attacher::AttachEngine3D
  Height = 30
  Placement = pos=(15,-8,15) rot=(0,1,0;1.5708rad)
  Radius = 2.65
FEATURE [Part::Cylinder] Cylinder054
  Angle = 360
  AttacherType = Attacher::AttachEngine3D
  Height = 30
  Placement = pos=(15,8,15) rot=(0,1,0;1.5708rad)
  Radius = 2.65
FEATURE [Part::Box] Box046  label="Cube046"
  AttacherType = Attacher::AttachEngine3D
  Height = 2
  Length = 30
  Placement = pos=(15,-4,14) rot=(0,0,1;0rad)
  Width = 9
FEATURE [Part::MultiFuse] Fusion020006007003002009018004004018
  Shapes = -> [Box046,Cylinder052,Cylinder051]
FEATURE [Part::MultiFuse] Fusion020006007003002009018004004019
  Shapes = -> [Cylinder054,Cylinder053]
FEATURE [Part::Cut] Cut019003008  label="back-30mm-spacer"
  Base = -> Fusion020006007003002009018004004018
  Tool = -> Fusion020006007003002009018004004019
FEATURE [Part::Box] Box047  label="Cube047"
  AttacherType = Attacher::AttachEngine3D
  Height = 2
  Length = 30
  Placement = pos=(15,-12,9) rot=(0,0,1;0rad)
  Width = 24
FEATURE [Part::Cut] Cut019003009
  Base = -> Cut019003008
  Tool = -> Box047
FEATURE [Part::Chamfer] Chamfer006038  label="back-30mm-spacer-trim"
  Base = -> Cut019003009
  Edges = 4 edges r=0.4: [Edge14,Edge16,Edge33,Edge39]
FEATURE [Part::Cylinder] Cylinder055
  Angle = 360
  AttacherType = Attacher::AttachEngine3D
  Height = 20
  Placement = pos=(8,8,0) rot=(0,0,1;0rad)
  Radius = 2.6
FEATURE [Part::Cylinder] Cylinder056
  Angle = 360
  AttacherType = Attacher::AttachEngine3D
  Height = 20
  Placement = pos=(-8,-8,0) rot=(0,0,1;0rad)
  Radius = 2.6
FEATURE [Part::Cylinder] Cylinder057
  Angle = 360
  AttacherType = Attacher::AttachEngine3D
  Height = 20
  Placement = pos=(8,8,0) rot=(0,0,1;0rad)
  Radius = 6
FEATURE [Part::Cylinder] Cylinder058
  Angle = 360
  AttacherType = Attacher::AttachEngine3D
  Height = 20
  Placement = pos=(-8,-8,0) rot=(0,0,1;0rad)
  Radius = 6
FEATURE [Part::Feature] Fusion020006007003002009018004004020001  label="Fusion020006007003002009018004004021"
  shape: bbox 30 x 30 x 20 mm, 8 faces (baked)
FEATURE [Part::Chamfer] Chamfer006039
  Base = -> Fusion020006007003002009018004004020001
  Edges = 17 edges r=1: [Edge1,Edge2,Edge3,Edge4,Edge5,Edge7,Edge8,Edge9,Edge10,Edge11,Edge12,Edge13,Edge14,Edge15,Edge16,Edge17,Edge18]
FEATURE [Part::Chamfer] Chamfer006040
  Base = -> Cylinder058
  Edges = 2 edges r=1: [Edge1,Edge3]
FEATURE [Part::Chamfer] Chamfer006041
  Base = -> Cylinder057
  Edges = 2 edges r=1: [Edge1,Edge3]
FEATURE [Part::MultiFuse] Fusion020006007003002009018004004020002
  Shapes = -> [Chamfer006041,Chamfer006040,Chamfer006039]
FEATURE [Part::MultiFuse] Fusion020006007003002009018004004020003
  Shapes = -> [Cylinder056,Cylinder055]
FEATURE [Part::Cut] Cut019003010  label="corner-mid"
  Base = -> Fusion020006007003002009018004004020002
  Tool = -> Fusion020006007003002009018004004020003
FEATURE [Part::Feature] Cut019003010001  label="Cut019003011"
  shape: bbox 30 x 30 x 20 mm, 53 faces (baked)
FEATURE [Part::Chamfer] Chamfer006042
  Base = -> Cut019003010001
  Edges = 4 edges r=1: [Edge108,Edge109,Edge110,Edge112]
FEATURE [Part::Feature] Fusion020006007003002009018004004020004  label="_M3-self-tapping009"
  Placement = pos=(0,6,10) rot=(-1,0,0;1.5708rad)
  shape: bbox 6 x 13 x 6 mm, 5 faces (baked)
FEATURE [Part::Feature] Fusion020006007003002009018004004020005  label="_M3-self-tapping010"
  Placement = pos=(-6,0,10) rot=(0,-1,0;1.5708rad)
  shape: bbox 13 x 6 x 6 mm, 5 faces (baked)
FEATURE [Part::MultiFuse] Fusion020006007003002009018004004020006
  Shapes = -> [Fusion020006007003002009018004004020005,Fusion020006007003002009018004004020004]
FEATURE [Part::Cut] Cut019003010002
  Base = -> Chamfer006042
  Tool = -> Fusion020006007003002009018004004020006
FEATURE [Part::Chamfer] Chamfer006043
  Base = -> Cut019003010002
  Edges = 2 edges r=0.4: [Edge73,Edge78]
FEATURE [Part::Cylinder] Cylinder059
  Angle = 360
  AttacherType = Attacher::AttachEngine3D
  Height = 40
  Placement = pos=(8,8,0) rot=(0,0,1;0rad)
  Radius = 5
FEATURE [Part::Cylinder] Cylinder060
  Angle = 360
  AttacherType = Attacher::AttachEngine3D
  Height = 40
  Placement = pos=(-8,-8,0) rot=(0,0,1;0rad)
  Radius = 5
FEATURE [Part::Box] Box048  label="Cube048"
  AttacherType = Attacher::AttachEngine3D
  Height = 40
  Length = 2
  Placement = pos=(-15,-15,0) rot=(0,0,1;0rad)
  Width = 30
FEATURE [Part::Box] Box049  label="Cube049"
  AttacherType = Attacher::AttachEngine3D
  Height = 40
  Length = 30
  Placement = pos=(-15,13,0) rot=(0,0,1;0rad)
  Width = 2
FEATURE [Part::Cylinder] Cylinder061
  Angle = 360
  AttacherType = Attacher::AttachEngine3D
  Height = 40
  Placement = pos=(-8,-8,0) rot=(0,0,1;0rad)
  Radius = 2.65
FEATURE [Part::Cylinder] Cylinder062
  Angle = 360
  AttacherType = Attacher::AttachEngine3D
  Height = 40
  Placement = pos=(8,8,0) rot=(0,0,1;0rad)
  Radius = 2.65
FEATURE [Part::Box] Box050  label="Cube050"
  AttacherType = Attacher::AttachEngine3D
  Height = 40
  Length = 14
  Placement = pos=(-4.24264,-5.65685,0) rot=(0,0,1;0.785398rad)
  Width = 2
FEATURE [Part::Box] Box051  label="Cube051"
  AttacherType = Attacher::AttachEngine3D
  Height = 40
  Length = 2
  Placement = pos=(-14,-9,0) rot=(0,0,1;0rad)
  Width = 2
FEATURE [Part::Box] Box052  label="Cube052"
  AttacherType = Attacher::AttachEngine3D
  Height = 40
  Length = 2
  Placement = pos=(7,12,0) rot=(0,0,1;0rad)
  Width = 2
FEATURE [Part::MultiFuse] Fusion020006007003002009018004004020007
  Shapes = -> [Box048,Box049]
FEATURE [Part::Chamfer] Chamfer006044
  Base = -> Fusion020006007003002009018004004020007
  Edges = 3 edges r=1: [Edge4,Edge9,Edge27]
FEATURE [Part::MultiFuse] Fusion020006007003002009018004004020008
  Shapes = -> [Chamfer006044,Box052,Box051,Box050,Cylinder059,Cylinder060]
FEATURE [Part::MultiFuse] Fusion020006007003002009018004004020009
  Shapes = -> [Cylinder061,Cylinder062]
FEATURE [Part::Cut] Cut019003010003  label="corner-40mm-wall"
  Base = -> Fusion020006007003002009018004004020008
  Tool = -> Fusion020006007003002009018004004020009
FEATURE [Part::Cylinder] Cylinder063
  Angle = 360
  AttacherType = Attacher::AttachEngine3D
  Height = 20
  Placement = pos=(-8,-15,23) rot=(1,0,0;1.5708rad)
  Radius = 2.6
FEATURE [Part::Cylinder] Cylinder064
  Angle = 360
  AttacherType = Attacher::AttachEngine3D
  Height = 20
  Placement = pos=(8,-15,23) rot=(1,0,0;1.5708rad)
  Radius = 2.6
FEATURE [Part::Feature] Fusion020006007003002009018004004020010001  label="Fusion020006007003002009018004004020011"
  shape: bbox 25 x 20 x 20 mm, 8 faces (baked)
FEATURE [Part::Chamfer] Chamfer006045
  Base = -> Fusion020006007003002009018004004020010001
  Edges = 17 edges r=1: [Edge1,Edge2,Edge3,Edge4,Edge5,Edge7,Edge8,Edge9,Edge10,Edge11,Edge12,Edge13,Edge14,Edge15,Edge16,Edge17,Edge18]
FEATURE [Part::Cylinder] Cylinder065
  Angle = 360
  AttacherType = Attacher::AttachEngine3D
  Height = 20
  Placement = pos=(8,-15,23) rot=(1,0,0;1.5708rad)
  Radius = 6
FEATURE [Part::Cylinder] Cylinder066
  Angle = 360
  AttacherType = Attacher::AttachEngine3D
  Height = 20
  Placement = pos=(-8,-15,23) rot=(1,0,0;1.5708rad)
  Radius = 6
FEATURE [Part::Chamfer] Chamfer006046
  Base = -> Cylinder065
  Edges = 2 edges r=1: [Edge1,Edge3]
FEATURE [Part::Chamfer] Chamfer006047
  Base = -> Cylinder066
  Edges = 2 edges r=1: [Edge1,Edge3]
FEATURE [Part::MultiFuse] Fusion020006007003002009018004004020010002
  Shapes = -> [Chamfer006045,Chamfer006047,Chamfer006046]
FEATURE [Part::MultiFuse] Fusion020006007003002009018004004020010003
  Shapes = -> [Cylinder064,Cylinder063]
FEATURE [Part::Cut] Cut019003010004
  Base = -> Fusion020006007003002009018004004020010002
  Tool = -> Fusion020006007003002009018004004020010003
FEATURE [Part::Feature] Cut019003010004001  label="Cut019003010005"
  shape: bbox 29 x 20 x 20 mm, 44 faces (baked)
FEATURE [Part::Chamfer] Chamfer006048
  Base = -> Cut019003010004001
  Edges = 4 edges r=1: [Edge89,Edge90,Edge92,Edge94]
FEATURE [Part::Cylinder] Cylinder067
  Angle = 360
  AttacherType = Attacher::AttachEngine3D
  Height = 20
  Placement = pos=(15,8,15) rot=(0,1,0;1.5708rad)
  Radius = 2.6
FEATURE [Part::Cylinder] Cylinder068
  Angle = 360
  AttacherType = Attacher::AttachEngine3D
  Height = 20
  Placement = pos=(15,-8,15) rot=(0,1,0;1.5708rad)
  Radius = 2.6
FEATURE [Part::Cylinder] Cylinder069
  Angle = 360
  AttacherType = Attacher::AttachEngine3D
  Height = 20
  Placement = pos=(15,8,15) rot=(0,1,0;1.5708rad)
  Radius = 6
FEATURE [Part::Cylinder] Cylinder070
  Angle = 360
  AttacherType = Attacher::AttachEngine3D
  Height = 20
  Placement = pos=(15,-8,15) rot=(0,1,0;1.5708rad)
  Radius = 6
FEATURE [Part::MultiFuse] Fusion020006007003002009018004004020010004
  Shapes = -> [Cylinder070,Cylinder069]
FEATURE [Part::Box] Box055  label="Cube055"
  AttacherType = Attacher::AttachEngine3D
  Height = 8
  Length = 20
  Placement = pos=(15,-10,19) rot=(0,0,1;0rad)
  Width = 4
FEATURE [Part::Chamfer] Chamfer006049
  Base = -> Fusion020006007003002009018004004020010004
  Edges = 4 edges r=1: [Edge1,Edge3,Edge4,Edge6]
FEATURE [Part::Feature] Fusion020006007003002009018004004020010005001  label="Fusion020006007003002009018004004020010006"
  shape: bbox 20 x 30 x 30 mm, 8 faces (baked)
FEATURE [Part::Chamfer] Chamfer006051
  Base = -> Box055
  Edges = 4 edges r=1: [Edge1,Edge3,Edge5,Edge7]
FEATURE [Part::MultiFuse] Fusion020006007003002009018004004020010005003
  Shapes = -> [Cylinder068,Cylinder067]
FEATURE [Part::Feature] Fusion020006007003002009018004004020010005004  label="_M3-self-tapping011"
  Placement = pos=(-6,-25,15) rot=(0,-1,0;1.5708rad)
  shape: bbox 13 x 6 x 6 mm, 5 faces (baked)
FEATURE [Part::Feature] Fusion020006007003002009018004004020010005005  label="_M3-self-tapping012"
  Placement = pos=(0,-25,21) rot=(0,0,1;0rad)
  shape: bbox 6 x 6 x 13 mm, 5 faces (baked)
FEATURE [Part::MultiFuse] Fusion020006007003002009018004004020010005006
  Shapes = -> [Fusion020006007003002009018004004020010005005,Fusion020006007003002009018004004020010005004]
FEATURE [Part::Feature] Fusion020006007003002009018004004020010005007  label="_M3-self-tapping013"
  Placement = pos=(25,0,21) rot=(0,0,1;0rad)
  shape: bbox 6 x 6 x 13 mm, 5 faces (baked)
FEATURE [Part::Feature] Fusion020006007003002009018004004020010005008  label="_M3-self-tapping014"
  Placement = pos=(25,6,23) rot=(-1,0,0;1.5708rad)
  shape: bbox 6 x 13 x 6 mm, 5 faces (baked)
FEATURE [Part::Feature] Fusion020006007003002009018004004020010005009  label="_M3-self-tapping015"
  Placement = pos=(25,6,7) rot=(-1,0,0;1.5708rad)
  shape: bbox 6 x 13 x 6 mm, 5 faces (baked)
FEATURE [Part::MultiFuse] Fusion020006007003002009018004004020010005010
  Shapes = -> [Fusion020006007003002009018004004020010005009,Fusion020006007003002009018004004020010005007,Fusion020006007003002009018004004020010005008]
FEATURE [Part::Box] Box056  label="Cube056"
  AttacherType = Attacher::AttachEngine3D
  Height = 15
  Length = 20
  Placement = pos=(15,10,0) rot=(0,0,1;0rad)
  Width = 10
FEATURE [Part::Cut] Cut019003010004002005002
  Base = -> Chamfer006048
  Tool = -> Fusion020006007003002009018004004020010005006
FEATURE [Part::Chamfer] Chamfer006055  label="top-side-mid-block"
  Base = -> Cut019003010004002005002
  Edges = 2 edges r=0.4: [Edge47,Edge72]
FEATURE [Part::Box] Box057  label="Cube057"
  AttacherType = Attacher::AttachEngine3D
  Height = 15
  Length = 20
  Placement = pos=(15,-20,20) rot=(0,0,1;0rad)
  Width = 10
FEATURE [Part::Cut] Cut019003010004002005003
  Base = -> Fusion020006007003002009018004004020010005001
  Tool = -> Box057
FEATURE [Part::Cut] Cut019003010004002005004
  Base = -> Cut019003010004002005003
  Tool = -> Box056
FEATURE [Part::Chamfer] Chamfer006056
  Base = -> Cut019003010004002005004
  Edges = 17 edges r=1: [Edge1,Edge3,Edge4,Edge5,Edge6,Edge7,Edge8,Edge9,Edge10,Edge11,Edge12,Edge13,Edge14,Edge15,Edge16,Edge17,Edge18]
FEATURE [Part::MultiFuse] Fusion020006007003002009018004004020010005011
  Shapes = -> [Chamfer006051,Chamfer006049,Chamfer006056]
FEATURE [Part::Cut] Cut019003010004002005005
  Base = -> Fusion020006007003002009018004004020010005011
  Tool = -> Fusion020006007003002009018004004020010005003
FEATURE [Part::Cut] Cut019003010004002005006
  Base = -> Cut019003010004002005005
  Tool = -> Fusion020006007003002009018004004020010005010
FEATURE [Part::Chamfer] Chamfer006057
  Base = -> Cut019003010004002005006
  Edges = 2 edges r=0.4: [Edge62,Edge68]
FEATURE [Part::Feature] Chamfer006057001  label="Chamfer006058"
  shape: bbox 20 x 29 x 21 mm, 47 faces (baked)
FEATURE [Part::Chamfer] Chamfer006057002  label="top-fb-mid-block"
  Base = -> Chamfer006057001
  Edges = 4 edges r=1: [Edge94,Edge95,Edge96,Edge98]
FEATURE [Part::Cylinder] Cylinder071
  Angle = 360
  AttacherType = Attacher::AttachEngine3D
  Height = 119.5
  Placement = pos=(-8,-15,23) rot=(1,0,0;1.5708rad)
  Radius = 2.65
FEATURE [Part::Cylinder] Cylinder072
  Angle = 360
  AttacherType = Attacher::AttachEngine3D
  Height = 119.5
  Placement = pos=(8,-15,23) rot=(1,0,0;1.5708rad)
  Radius = 2.65
FEATURE [Part::Box] Box058  label="Cube058"
  AttacherType = Attacher::AttachEngine3D
  Height = 20
  Length = 2
  Placement = pos=(-15,-134.5,10) rot=(0,0,1;0rad)
  Width = 119.5
FEATURE [Part::Box] Box059  label="Cube059"
  AttacherType = Attacher::AttachEngine3D
  Height = 2
  Length = 25
  Placement = pos=(-15,-134.5,28) rot=(0,0,1;0rad)
  Width = 119.5
FEATURE [Part::Cylinder] Cylinder073
  Angle = 360
  AttacherType = Attacher::AttachEngine3D
  Height = 119.5
  Placement = pos=(-8,-15,23) rot=(1,0,0;1.5708rad)
  Radius = 5
FEATURE [Part::Cylinder] Cylinder074
  Angle = 360
  AttacherType = Attacher::AttachEngine3D
  Height = 119.5
  Placement = pos=(8,-15,23) rot=(1,0,0;1.5708rad)
  Radius = 5
FEATURE [Part::Box] Box060  label="Cube060"
  AttacherType = Attacher::AttachEngine3D
  Height = 2
  Length = 2
  Placement = pos=(-14,-134.5,22) rot=(0,0,1;0rad)
  Width = 119.5
FEATURE [Part::Box] Box061  label="Cube061"
  AttacherType = Attacher::AttachEngine3D
  Height = 2
  Length = 2
  Placement = pos=(-9,-134.5,27) rot=(0,0,1;0rad)
  Width = 119.5
FEATURE [Part::Box] Box062  label="Cube062"
  AttacherType = Attacher::AttachEngine3D
  Height = 2
  Length = 2
  Placement = pos=(7,-134.5,27) rot=(0,0,1;0rad)
  Width = 119.5
FEATURE [Part::MultiFuse] Fusion020006007003002009018004004020010005015
  Shapes = -> [Box058,Box059]
FEATURE [Part::Chamfer] Chamfer006057003
  Base = -> Fusion020006007003002009018004004020010005015
  Edges = 3 edges r=1: [Edge4,Edge9,Edge27]
FEATURE [Part::MultiFuse] Fusion020006007003002009018004004020010005016
  Shapes = -> [Cylinder074,Cylinder073,Box062,Box061,Box060,Chamfer006057003]
FEATURE [Part::MultiFuse] Fusion020006007003002009018004004020010005017
  Shapes = -> [Cylinder072,Cylinder071]
FEATURE [Part::Cut] Cut019003010004002005007  label="top-side-120mm-wall"
  Base = -> Fusion020006007003002009018004004020010005016
  Tool = -> Fusion020006007003002009018004004020010005017
FEATURE [Part::Feature] Cut019003010004002005007001  label="top-side-120mm-wall001"
  shape: bbox 28 x 119.5 x 20 mm, 25 faces (baked)
FEATURE [Part::Box] Box063  label="Cube063"
  AttacherType = Attacher::AttachEngine3D
  Height = 2
  Length = 7
  Placement = pos=(-3.5,-56,22) rot=(0,0,1;0rad)
  Width = 41
FEATURE [Part::Box] Box064  label="Cube064"
  AttacherType = Attacher::AttachEngine3D
  Height = 2.5
  Length = 11
  Placement = pos=(-10.5,-51.5,27.5) rot=(0,0,1;0rad)
  Width = 37
FEATURE [Part::Cut] Cut019003010004002005007002
  Base = -> Cut019003010004002005007001
  Tool = -> Box064
FEATURE [Part::Chamfer] Chamfer006057004
  Base = -> Cut019003010004002005007002
  Edges = 1 edges r=2: [Edge88]
FEATURE [Part::Cylinder] Cylinder075
  Angle = 360
  AttacherType = Attacher::AttachEngine3D
  Height = 124.5
  Placement = pos=(15,-8,15) rot=(0,1,0;1.5708rad)
  Radius = 5
FEATURE [Part::Cylinder] Cylinder076
  Angle = 360
  AttacherType = Attacher::AttachEngine3D
  Height = 124.5
  Placement = pos=(15,8,15) rot=(0,1,0;1.5708rad)
  Radius = 5
FEATURE [Part::Cylinder] Cylinder077
  Angle = 360
  AttacherType = Attacher::AttachEngine3D
  Height = 124.5
  Placement = pos=(15,8,15) rot=(0,1,0;1.5708rad)
  Radius = 2.65
FEATURE [Part::Cylinder] Cylinder078
  Angle = 360
  AttacherType = Attacher::AttachEngine3D
  Height = 124.5
  Placement = pos=(15,-8,15) rot=(0,1,0;1.5708rad)
  Radius = 2.65
FEATURE [Part::Box] Box065  label="Cube065"
  AttacherType = Attacher::AttachEngine3D
  Height = 10
  Length = 124.5
  Placement = pos=(15,-9,19) rot=(0,0,1;0rad)
  Width = 2
FEATURE [Part::Box] Box066  label="Cube066"
  AttacherType = Attacher::AttachEngine3D
  Height = 15
  Length = 124.5
  Placement = pos=(15,13,15) rot=(0,0,1;0rad)
  Width = 2
FEATURE [Part::Box] Box067  label="Cube067"
  AttacherType = Attacher::AttachEngine3D
  Height = 2
  Length = 124.5
  Placement = pos=(15,-10,28) rot=(0,0,1;0rad)
  Width = 25
FEATURE [Part::Box] Box068  label="Cube068"
  AttacherType = Attacher::AttachEngine3D
  Height = 2
  Length = 124.5
  Placement = pos=(15,12,15) rot=(0,0,1;0rad)
  Width = 2
FEATURE [Part::Box] Box069  label="Cube069"
  AttacherType = Attacher::AttachEngine3D
  Height = 2
  Length = 124.5
  Placement = pos=(15,-4,14) rot=(0,0,1;0rad)
  Width = 8
FEATURE [Part::MultiFuse] Fusion020006007003002009018004004020010005019
  Shapes = -> [Box067,Box066]
FEATURE [Part::Chamfer] Chamfer006057005
  Base = -> Fusion020006007003002009018004004020010005019
  Edges = 3 edges r=1: [Edge7,Edge15,Edge27]
FEATURE [Part::MultiFuse] Fusion020006007003002009018004004020010005020
  Shapes = -> [Cylinder075,Box065,Chamfer006057005,Box069,Box068,Cylinder076]
FEATURE [Part::MultiFuse] Fusion020006007003002009018004004020010005021
  Shapes = -> [Cylinder078,Cylinder077]
FEATURE [Part::Cut] Cut019003010004002005007003  label="top-fb-125mm-wall"
  Base = -> Fusion020006007003002009018004004020010005020
  Tool = -> Fusion020006007003002009018004004020010005021
FEATURE [Part::Box] Box070  label="Cube070"
  AttacherType = Attacher::AttachEngine3D
  Height = 4
  Length = 6.5
  Placement = pos=(-15,-40,29) rot=(0,0,1;0rad)
  Width = 10
FEATURE [Part::Box] Box071  label="Cube071"
  AttacherType = Attacher::AttachEngine3D
  Height = 4
  Length = 10
  Placement = pos=(-5,-45,29) rot=(0,0,1;0rad)
  Width = 5
FEATURE [Part::Chamfer] Chamfer006057007
  Base = -> Box070
  Edges = 5 edges r=1: [Edge1,Edge2,Edge3,Edge10,Edge12]
  Placement = pos=(0,14,0) rot=(0,0,1;0rad)
FEATURE [Part::Feature] Part__Mirroring001  label="top-cube-base002 (Mirror #1)001"
  shape: bbox 30 x 30 x 30 mm, 85 faces (baked)
FEATURE [Part::Cylinder] Cylinder079
  Angle = 360
  AttacherType = Attacher::AttachEngine3D
  Height = 26
  Placement = pos=(-8,-15,23) rot=(1,0,0;1.5708rad)
  Radius = 2.65
FEATURE [Part::Cylinder] Cylinder080
  Angle = 360
  AttacherType = Attacher::AttachEngine3D
  Height = 26
  Placement = pos=(8,-15,23) rot=(1,0,0;1.5708rad)
  Radius = 2.65
FEATURE [Part::Box] Box072  label="Cube072"
  AttacherType = Attacher::AttachEngine3D
  Height = 35
  Length = 3
  Placement = pos=(-21.5,-41,-5) rot=(0,0,1;0rad)
  Width = 26
FEATURE [Part::Cylinder] Cylinder081
  Angle = 360
  AttacherType = Attacher::AttachEngine3D
  Height = 26
  Placement = pos=(-8,-15,23) rot=(1,0,0;1.5708rad)
  Radius = 6
FEATURE [Part::Cylinder] Cylinder082
  Angle = 360
  AttacherType = Attacher::AttachEngine3D
  Height = 26
  Placement = pos=(8,-15,23) rot=(1,0,0;1.5708rad)
  Radius = 6
FEATURE [Part::Box] Box073  label="Cube073"
  AttacherType = Attacher::AttachEngine3D
  Height = 35
  Length = 3
  Placement = pos=(-15,-41,-5) rot=(0,0,1;0rad)
  Width = 26
FEATURE [Part::Box] Box074  label="Cube074"
  AttacherType = Attacher::AttachEngine3D
  Height = 3
  Length = 30
  Placement = pos=(-20,-41,27) rot=(0,0,1;0rad)
  Width = 26
FEATURE [Part::Box] Box075  label="Cube075"
  AttacherType = Attacher::AttachEngine3D
  Height = 16
  Length = 3
  Placement = pos=(-21.5,-38,1) rot=(0,0,1;0rad)
  Width = 20
FEATURE [Part::Box] Box076  label="Cube076"
  AttacherType = Attacher::AttachEngine3D
  Height = 16
  Length = 3
  Placement = pos=(-15,-38,1) rot=(0,0,1;0rad)
  Width = 20
FEATURE [Part::Cut] Cut019003010004002005007004
  Base = -> Box073
  Tool = -> Box076
FEATURE [Part::Cut] Cut019003010004002005007005
  Base = -> Box072
  Tool = -> Box075
FEATURE [Part::MultiFuse] Fusion020006007003002009018004004020010005023
  Shapes = -> [Box074,Cut019003010004002005007005,Cut019003010004002005007004]
FEATURE [Part::Chamfer] Chamfer006057009
  Base = -> Fusion020006007003002009018004004020010005023
  Edges = 4 edges r=2: [Edge8,Edge30,Edge54,Edge63]
FEATURE [Part::Chamfer] Chamfer006057010
  Base = -> Chamfer006057009
  Edges = 8 edges r=1: [Edge37,Edge38,Edge39,Edge40,Edge73,Edge75,Edge76,Edge78]
FEATURE [Part::Feature] Chamfer006057010001  label="Chamfer006057011"
  shape: bbox 31.5 x 26 x 35 mm, 32 faces (baked)
FEATURE [Part::Chamfer] Chamfer006057010002
  Base = -> Chamfer006057010001
  Edges = 2 edges r=1: [Edge42,Edge87]
FEATURE [Part::Chamfer] Chamfer006057010003
  Base = -> Chamfer006057010002
  Edges = 13 edges r=0.4: [Edge1,Edge3,Edge4,Edge5,Edge6,Edge15,Edge16,Edge18,Edge20,Edge27,Edge31,Edge33,Edge35]
FEATURE [Part::Chamfer] Chamfer006057010004
  Base = -> Chamfer006057010003
  Edges = 8 edges r=0.4: [Edge7,Edge8,Edge9,Edge10,Edge11,Edge12,Edge13,Edge14]
FEATURE [Part::MultiFuse] Fusion020006007003002009018004004020010005024
  Shapes = -> [Cylinder081,Cylinder082]
FEATURE [Part::Chamfer] Chamfer006057010005
  Base = -> Fusion020006007003002009018004004020010005024
  Edges = 4 edges r=1: [Edge1,Edge3,Edge4,Edge6]
FEATURE [Part::MultiFuse] Fusion020006007003002009018004004020010005025
  Shapes = -> [Cylinder080,Cylinder079]
FEATURE [Part::Cut] Cut019003010004002005007006
  Base = -> Chamfer006057010005
  Tool = -> Fusion020006007003002009018004004020010005025
FEATURE [Part::MultiFuse] Fusion020006007003002009018004004020010005026
  Shapes = -> [Chamfer006057010004,Cut019003010004002005007006]
FEATURE [Part::Feature] Fusion020006007003002009018004004020010005027  label="_M3-self-tapping016"
  Placement = pos=(-16,-20,-2) rot=(0,1,0;1.5708rad)
  shape: bbox 13 x 6 x 6 mm, 5 faces (baked)
FEATURE [Part::Feature] Fusion020006007003002010001  label="_M3-outer-slot001"
  Placement = pos=(-17,-20,-2) rot=(0,-1,0;1.5708rad)
  shape: bbox 13 x 6 x 6 mm, 5 faces (baked)
FEATURE [Part::Feature] Fusion020006007003002009018004004020010005028  label="_M3-outer-slot002"
  Placement = pos=(-17,-36,-2) rot=(0,-1,0;1.5708rad)
  shape: bbox 13 x 6 x 6 mm, 5 faces (baked)
FEATURE [Part::MultiFuse] Fusion020006007003002009018004004020010005029
  Shapes = -> [Fusion020006007003002010001,Fusion020006007003002009018004004020010005028]
FEATURE [Part::Cut] Cut019003010004002005007007
  Base = -> Fusion020006007003002009018004004020010005026
  Tool = -> Fusion020006007003002009018004004020010005029
FEATURE [Part::Feature] Fusion020006007003002009018004004020010005030  label="_M3-self-tapping017"
  Placement = pos=(-16,-36,-2) rot=(0,1,0;1.5708rad)
  shape: bbox 13 x 6 x 6 mm, 5 faces (baked)
FEATURE [Part::MultiFuse] Fusion020006007003002009018004004020010005031
  Shapes = -> [Fusion020006007003002009018004004020010005030,Fusion020006007003002009018004004020010005027]
FEATURE [Part::Cut] Cut019003010004002005007008  label="bowden-door-rev"
  Base = -> Cut019003010004002005007007
  Tool = -> Fusion020006007003002009018004004020010005031
FEATURE [Part::Box] Box077  label="Cube077"
  AttacherType = Attacher::AttachEngine3D
  Height = 20
  Length = 28
  Placement = pos=(-15,-85,10) rot=(0,0,1;0rad)
  Width = 55.5
FEATURE [Part::Box] Box078  label="Cube078"
  AttacherType = Attacher::AttachEngine3D
  Height = 20
  Length = 28
  Placement = pos=(-15,-53,10) rot=(0,0,1;0rad)
  Width = 38
FEATURE [Part::Feature] Fusion020006007003002009018004004020010005018001  label="top-side-cutout-120mm-wall001"
  shape: bbox 28 x 120 x 20 mm, 37 faces (baked)
FEATURE [Part::MultiCommon] Common  label="top-side-cutout-38mm-wall"
  Shapes = -> [Fusion020006007003002009018004004020010005018001,Box078]
FEATURE [Part::Feature] Cut019003010004002005007009  label="top-side-120mm-wall002"
  shape: bbox 28 x 119.5 x 20 mm, 25 faces (baked)
FEATURE [Part::MultiCommon] Common001  label="top-side-56mm-wall"
  Shapes = -> [Cut019003010004002005007009,Box077]
FEATURE [Part::MultiFuse] Fusion020006007003002009018004004020010005018002  label="top-side-cutout-120mm-wall"
  Shapes = -> [Box063,Chamfer006057004]
FEATURE [Part::Chamfer] Chamfer006057008
  Base = -> Box071
  Edges = 5 edges r=1: [Edge1,Edge2,Edge5,Edge6,Edge10]
  Placement = pos=(0,10,0) rot=(0,0,1;0rad)
FEATURE [Part::MultiFuse] Fusion020006007003002009018004004020010005018003  label="top-front-cube"
  Shapes = -> [Chamfer006057007,Part__Mirroring001,Chamfer006057008]
FEATURE [Part::Box] Box079  label="Cube079"
  AttacherType = Attacher::AttachEngine3D
  Height = 25
  Length = 50
  Placement = pos=(15,-13,-5) rot=(0,0,1;0rad)
  Width = 28
FEATURE [Part::MultiCommon] Common002  label="bottom-back-50mm-wall"
  Shapes = -> [Box079,Cut019003006]
FEATURE [Part::Feature] Common002001  label="bottom-back-50mm-wall001"
  shape: bbox 50 x 28 x 25 mm, 21 faces (baked)
FEATURE [Part::Box] Box080  label="Cube080"
  AttacherType = Attacher::AttachEngine3D
  Height = 30
  Length = 20
  Placement = pos=(20,-15,-5) rot=(0,0,1;0rad)
  Width = 30
FEATURE [Part::MultiCommon] Common002002  label="bottom-back-20mm-wall"
  Shapes = -> [Box080,Common002001]
FEATURE [Part::Feature] Common002002001  label="bottom-back-20mm-wall001"
  shape: bbox 20 x 28 x 25 mm, 21 faces (baked)
FEATURE [Part::Feature] Cut019003010003001  label="corner-40mm-wall001"
  Placement = pos=(0,0,15) rot=(0,0,1;0rad)
  shape: bbox 30 x 30 x 40 mm, 25 faces (baked)
FEATURE [Part::Feature] Cut019003010004002005007010  label="corner-40mm-wall002"
  shape: bbox 30 x 30 x 40 mm, 25 faces (baked)
FEATURE [Part::MultiFuse] Fusion020006007003002009018004004020010005018004  label="corner-55mm-wall"
  Shapes = -> [Cut019003010004002005007010,Cut019003010003001]
FEATURE [Part::Feature] Fusion020006007003002009018004004020010005018005  label="_M3-self-tapping018"
  Placement = pos=(-6,0,10) rot=(0,-1,0;1.5708rad)
  shape: bbox 13 x 6 x 6 mm, 5 faces (baked)
FEATURE [Part::Feature] Fusion020006007003002009018004004020010005018006  label="_M3-self-tapping019"
  Placement = pos=(0,6,10) rot=(-1,0,0;1.5708rad)
  shape: bbox 6 x 13 x 6 mm, 5 faces (baked)
FEATURE [Part::MultiFuse] Fusion020006007003002009018004004020010005018007
  Shapes = -> [Fusion020006007003002009018004004020010005018005,Fusion020006007003002009018004004020010005018006]
FEATURE [Part::Cut] Cut019003010004002005007011
  Base = -> Cut019003010
  Tool = -> Fusion020006007003002009018004004020010005018007
FEATURE [Part::Chamfer] Chamfer006057010006
  Base = -> Cut019003010004002005007011
  Edges = 2 edges r=0.4: [Edge30,Edge56]
FEATURE [Part::Feature] Chamfer006057010006001  label="Chamfer006057010007"
  shape: bbox 30 x 30 x 20 mm, 57 faces (baked)
FEATURE [Part::Chamfer] Chamfer006057010006002  label="corner-mid-block"
  Base = -> Chamfer006057010006001
  Edges = 4 edges r=1: [Edge118,Edge119,Edge120,Edge122]
FEATURE [Part::Feature] Cut019002001  label="bottom-side-mid-block001"
  Placement = pos=(0,35,0) rot=(0,0,1;0rad)
  shape: bbox 30 x 20 x 25 mm, 64 faces (baked)
FEATURE [Part::Box] Box082  label="Cube082"
  AttacherType = Attacher::AttachEngine3D
  Height = 11
  Length = 6
  Placement = pos=(-3,0,-10) rot=(0,0,1;0rad)
  Width = 20
FEATURE [Part::Cylinder] Cylinder083
  Angle = 360
  AttacherType = Attacher::AttachEngine3D
  Height = 10
  Placement = pos=(-10,10,15) rot=(0,-1,0;1.5708rad)
  Radius = 2
FEATURE [Part::Cut] Cut019003010004002005007012
  Base = -> Cut019002001
  Tool = -> Cylinder083
FEATURE [Part::Box] Box083  label="Cube083"
  AttacherType = Attacher::AttachEngine3D
  Height = 5
  Length = 3
  Placement = pos=(-15,-40,10) rot=(0,0,1;0rad)
  Width = 25
FEATURE [Part::Chamfer] Chamfer006057010006005
  Base = -> Box083
  Edges = 2 edges r=1: [Edge10,Edge12]
FEATURE [Part::Feature] Cut018001  label="side-stopper001"
  shape: bbox 30 x 25 x 22 mm, 44 faces (baked)
FEATURE [Part::MultiFuse] Fusion020006007003002009018004004020010005018010  label="side-stopper-raised"
  Shapes = -> [Chamfer006057010006005,Cut018001]
FEATURE [Part::Feature] Cut019003002001  label="bottom-fb-mid-block001"
  shape: bbox 20 x 30 x 26 mm, 64 faces (baked)
FEATURE [Part::Feature] Chamfer006057002001  label="top-fb-mid-block001"
  Placement = pos=(0,0,-9) rot=(0,0,1;0rad)
  shape: bbox 20 x 29 x 21 mm, 51 faces (baked)
FEATURE [Part::Chamfer] Chamfer006057010006006
  Base = -> Box082
  Edges = 8 edges r=1: [Edge1,Edge3,Edge4,Edge5,Edge7,Edge8,Edge9,Edge11]
FEATURE [Part::MultiFuse] Fusion020006007003002009018004004020010005018011  label="bottom-side-mid-block-rf"
  Shapes = -> [Cut019003010004002005007012,Chamfer006057010006006]
FEATURE [Part::Cylinder] Cylinder084
  Angle = 360
  AttacherType = Attacher::AttachEngine3D
  Height = 17
  Placement = pos=(20.5,0,0) rot=(0,0,1;0rad)
  Radius = 5.5
FEATURE [Part::Cylinder] Cylinder085
  Angle = 360
  AttacherType = Attacher::AttachEngine3D
  Height = 17
  Placement = pos=(29.5,0,0) rot=(0,0,1;0rad)
  Radius = 5.5
FEATURE [Part::Cylinder] Cylinder086
  Angle = 360
  AttacherType = Attacher::AttachEngine3D
  Height = 16
  Placement = pos=(29.5,0,0) rot=(0,0,1;0rad)
  Radius = 2.6
FEATURE [Part::Cylinder] Cylinder087
  Angle = 360
  AttacherType = Attacher::AttachEngine3D
  Height = 16
  Placement = pos=(20.5,0,0) rot=(0,0,1;0rad)
  Radius = 2.6
FEATURE [Part::Cylinder] Cylinder088
  Angle = 360
  AttacherType = Attacher::AttachEngine3D
  Height = 17
  Placement = pos=(20.5,0,4) rot=(0,0,1;0rad)
  Radius = 2.6
FEATURE [Part::Cylinder] Cylinder089
  Angle = 360
  AttacherType = Attacher::AttachEngine3D
  Height = 17
  Placement = pos=(29.5,0,4) rot=(0,0,1;0rad)
  Radius = 2.6
FEATURE [Part::Cylinder] Cylinder090
  Angle = 360
  AttacherType = Attacher::AttachEngine3D
  Height = 17
  Placement = pos=(29.5,0,4) rot=(0,0,1;0rad)
  Radius = 5.5
FEATURE [Part::Cylinder] Cylinder091
  Angle = 360
  AttacherType = Attacher::AttachEngine3D
  Height = 17
  Placement = pos=(20.5,0,4) rot=(0,0,1;0rad)
  Radius = 5.5
FEATURE [Part::Chamfer] Chamfer006057010006007
  Base = -> Cylinder091
  Edges = 1 edges r=1: [Edge1]
FEATURE [Part::Chamfer] Chamfer006057010006008
  Base = -> Cylinder090
  Edges = 1 edges r=1: [Edge1]
FEATURE [Part::Cut] Cut019003010004002005007013
  Base = -> Chamfer006057010006007
  Tool = -> Cylinder088
FEATURE [Part::Cut] Cut019003010004002005007014
  Base = -> Chamfer006057010006008
  Tool = -> Cylinder089
FEATURE [Part::MultiFuse] Fusion020006007003002009018004004020010005018012
  Shapes = -> [Cut019003010004002005007013,Cut019003010004002005007014]
FEATURE [Part::Cylinder] Cylinder092
  Angle = 360
  AttacherType = Attacher::AttachEngine3D
  Height = 20
  Placement = pos=(15,8,15) rot=(0,1,0;1.5708rad)
  Radius = 2.7
FEATURE [Part::Cylinder] Cylinder093
  Angle = 360
  AttacherType = Attacher::AttachEngine3D
  Height = 20
  Placement = pos=(15,-8,15) rot=(0,1,0;1.5708rad)
  Radius = 2.7
FEATURE [Part::MultiFuse] Fusion020006007003002009018004004020010005018013
  Shapes = -> [Cylinder093,Cylinder092]
FEATURE [Part::Cut] Cut019003010004002005007015
  Base = -> Fusion020006007003002009018004004020010005018012
  Tool = -> Fusion020006007003002009018004004020010005018013
FEATURE [Part::Cylinder] Cylinder094
  Angle = 360
  AttacherType = Attacher::AttachEngine3D
  Height = 16
  Placement = pos=(20.5,0,5) rot=(0,0,1;0rad)
  Radius = 2.7
FEATURE [Part::Cylinder] Cylinder095
  Angle = 360
  AttacherType = Attacher::AttachEngine3D
  Height = 16
  Placement = pos=(29.5,0,5) rot=(0,0,1;0rad)
  Radius = 2.7
FEATURE [Part::MultiFuse] Fusion020006007003002009018004004020010005018014
  Shapes = -> [Cylinder095,Cylinder094]
FEATURE [Part::Cut] Cut019003010004002005007016
  Base = -> Cut019003002001
  Tool = -> Fusion020006007003002009018004004020010005018014
FEATURE [Part::MultiFuse] Fusion020006007003002009018004004020010005018015
  Shapes = -> [Cut019003010004002005007016,Cut019003010004002005007015]
FEATURE [Part::Box] Box084  label="Cube084"
  AttacherType = Attacher::AttachEngine3D
  Height = 11
  Length = 20
  Placement = pos=(15,-3,-10) rot=(0,0,1;0rad)
  Width = 6
FEATURE [Part::Chamfer] Chamfer006057010006009
  Base = -> Box084
  Edges = 8 edges r=1: [Edge1,Edge3,Edge4,Edge5,Edge7,Edge8,Edge9,Edge11]
FEATURE [Part::MultiFuse] Fusion020006007003002009018004004020010005018016  label="bottom-back-joiner"
  Shapes = -> [Fusion020006007003002009018004004020010005018015,Chamfer006057010006009]
FEATURE [Part::Chamfer] Chamfer006057010006010
  Base = -> Cylinder085
  Edges = 1 edges r=1: [Edge3]
FEATURE [Part::Chamfer] Chamfer006057010006011
  Base = -> Cylinder084
  Edges = 1 edges r=1: [Edge3]
FEATURE [Part::Cut] Cut019003010004002005007017
  Base = -> Chamfer006057010006011
  Tool = -> Cylinder087
FEATURE [Part::Cut] Cut019003010004002005007018
  Base = -> Chamfer006057010006010
  Tool = -> Cylinder086
FEATURE [Part::Chamfer] Chamfer006057010006012
  Base = -> Cut019003010004002005007018
  Edges = 1 edges r=1: [Edge6]
FEATURE [Part::Chamfer] Chamfer006057010006013
  Base = -> Cut019003010004002005007017
  Edges = 1 edges r=1: [Edge6]
FEATURE [Part::Cylinder] Cylinder096
  Angle = 360
  AttacherType = Attacher::AttachEngine3D
  Height = 16
  Placement = pos=(29.5,0,0) rot=(0,0,1;0rad)
  Radius = 2.7
FEATURE [Part::Cylinder] Cylinder097
  Angle = 360
  AttacherType = Attacher::AttachEngine3D
  Height = 16
  Placement = pos=(20.5,0,0) rot=(0,0,1;0rad)
  Radius = 2.7
FEATURE [Part::MultiFuse] Fusion020006007003002009018004004020010005018017
  Shapes = -> [Cylinder097,Cylinder096]
FEATURE [Part::Cut] Cut019003010004002005007019
  Base = -> Chamfer006057002001
  Tool = -> Fusion020006007003002009018004004020010005018017
FEATURE [Part::Cylinder] Cylinder098
  Angle = 360
  AttacherType = Attacher::AttachEngine3D
  Height = 20
  Placement = pos=(15,-8,6) rot=(0,1,0;1.5708rad)
  Radius = 2.7
FEATURE [Part::Cylinder] Cylinder099
  Angle = 360
  AttacherType = Attacher::AttachEngine3D
  Height = 20
  Placement = pos=(15,8,6) rot=(0,1,0;1.5708rad)
  Radius = 2.7
FEATURE [Part::MultiFuse] Fusion020006007003002009018004004020010005018018
  Shapes = -> [Cylinder099,Cylinder098]
FEATURE [Part::MultiFuse] Fusion020006007003002009018004004020010005018019
  Shapes = -> [Chamfer006057010006012,Chamfer006057010006013]
FEATURE [Part::Cut] Cut019003010004002005007020
  Base = -> Fusion020006007003002009018004004020010005018019
  Tool = -> Fusion020006007003002009018004004020010005018018
FEATURE [Part::MultiFuse] Fusion020006007003002009018004004020010005018020
  Shapes = -> [Cut019003010004002005007020,Cut019003010004002005007019]
FEATURE [Part::Feature] Fusion020006007003002009018004004020010005018021  label="_M3-self-tapping020"
  Placement = pos=(25,0,12) rot=(0,0,1;0rad)
  shape: bbox 6 x 6 x 13 mm, 5 faces (baked)
FEATURE [Part::Cut] Cut019003010004002005007021  label="top-back-joiner"
  Base = -> Fusion020006007003002009018004004020010005018020
  Tool = -> Fusion020006007003002009018004004020010005018021
FEATURE [Part::Feature] Chamfer006023001  label="fb-stopper001"
  shape: bbox 25 x 30 x 30 mm, 46 faces (baked)
FEATURE [Part::Cylinder] Cylinder100
  Angle = 360
  AttacherType = Attacher::AttachEngine3D
  Height = 5
  Placement = pos=(15,-8,15) rot=(0,1,0;1.5708rad)
  Radius = 4
FEATURE [Part::Cylinder] Cylinder101
  Angle = 360
  AttacherType = Attacher::AttachEngine3D
  Height = 5
  Placement = pos=(15,8,15) rot=(0,1,0;1.5708rad)
  Radius = 4
FEATURE [Part::Cylinder] Cylinder102
  Angle = 360
  AttacherType = Attacher::AttachEngine3D
  Height = 25
  Placement = pos=(15,8,15) rot=(0,1,0;1.5708rad)
  Radius = 1.7
FEATURE [Part::Cylinder] Cylinder103
  Angle = 360
  AttacherType = Attacher::AttachEngine3D
  Height = 25
  Placement = pos=(15,-8,15) rot=(0,1,0;1.5708rad)
  Radius = 1.7
FEATURE [Part::MultiFuse] Fusion020006007003002009018004004020010005018022
  Shapes = -> [Cylinder101,Cylinder100]
FEATURE [Part::MultiFuse] Fusion020006007003002009018004004020010005018023
  Shapes = -> [Chamfer006023001,Fusion020006007003002009018004004020010005018022]
FEATURE [Part::Cylinder] Cylinder104
  Angle = 360
  AttacherType = Attacher::AttachEngine3D
  Height = 25
  Placement = pos=(20,-8,15) rot=(0,1,0;1.5708rad)
  Radius = 3.5
FEATURE [Part::Cylinder] Cylinder105
  Angle = 360
  AttacherType = Attacher::AttachEngine3D
  Height = 25
  Placement = pos=(20,8,15) rot=(0,1,0;1.5708rad)
  Radius = 3.5
FEATURE [Part::MultiFuse] Fusion020006007003002009018004004020010005018024
  Shapes = -> [Cylinder105,Cylinder104]
FEATURE [Part::Cut] Cut019003010004002005007022
  Base = -> Fusion020006007003002009018004004020010005018023
  Tool = -> Fusion020006007003002009018004004020010005018024
FEATURE [Part::MultiFuse] Fusion020006007003002009018004004020010005018025
  Shapes = -> [Cylinder103,Cylinder102]
FEATURE [Part::Cut] Cut019003010004002005007023  label="back-stopper-bolt-on"
  Base = -> Cut019003010004002005007022
  Tool = -> Fusion020006007003002009018004004020010005018025
FEATURE [Part::Feature] Chamfer003001  label="bottom-cube001"
  shape: bbox 30 x 30 x 30 mm, 88 faces (baked)
FEATURE [Part::Cylinder] Cylinder106
  Angle = 360
  AttacherType = Attacher::AttachEngine3D
  Height = 6
  Placement = pos=(9,8,15) rot=(0,1,0;1.5708rad)
  Radius = 1.25
FEATURE [Part::Cylinder] Cylinder107
  Angle = 360
  AttacherType = Attacher::AttachEngine3D
  Height = 6
  Placement = pos=(9,-8,15) rot=(0,1,0;1.5708rad)
  Radius = 1.25
FEATURE [Part::Cylinder] Cylinder108
  Angle = 360
  AttacherType = Attacher::AttachEngine3D
  Height = 15
  Placement = pos=(-3e-15,-8,15) rot=(0,1,0;1.5708rad)
  Radius = 4
FEATURE [Part::Cylinder] Cylinder109
  Angle = 360
  AttacherType = Attacher::AttachEngine3D
  Height = 15
  Placement = pos=(-3e-15,8,15) rot=(0,1,0;1.5708rad)
  Radius = 4
FEATURE [Part::MultiFuse] Fusion020006007003002009018004004020010005018026
  Shapes = -> [Cylinder108,Cylinder109,Chamfer003001]
FEATURE [Part::MultiFuse] Fusion020006007003002009018004004020010005018027
  Shapes = -> [Cylinder107,Cylinder106]
FEATURE [Part::Cut] Cut019003010004002005007024
  Base = -> Fusion020006007003002009018004004020010005018026
  Tool = -> Fusion020006007003002009018004004020010005018027
FEATURE [Part::Chamfer] Chamfer006057010006014  label="bottom-bacl-cube-bolt-on"
  Base = -> Cut019003010004002005007024
  Edges = 2 edges r=0.4: [Edge8,Edge88]
FEATURE [Part::Cylinder] Cylinder110
  Angle = 360
  AttacherType = Attacher::AttachEngine3D
  Height = 4.4
  Placement = pos=(15,8,15) rot=(0,1,0;1.5708rad)
  Radius = 4
FEATURE [Part::Cylinder] Cylinder111
  Angle = 360
  AttacherType = Attacher::AttachEngine3D
  Height = 4.4
  Placement = pos=(15,-8,15) rot=(0,1,0;1.5708rad)
  Radius = 4
FEATURE [Part::MultiFuse] Fusion020006007003002009018004004020010005018028  label="bottom-back-joiner-corner"
  Shapes = -> [Fusion020006007003002009018004004020010005018016,Cylinder110,Cylinder111]
